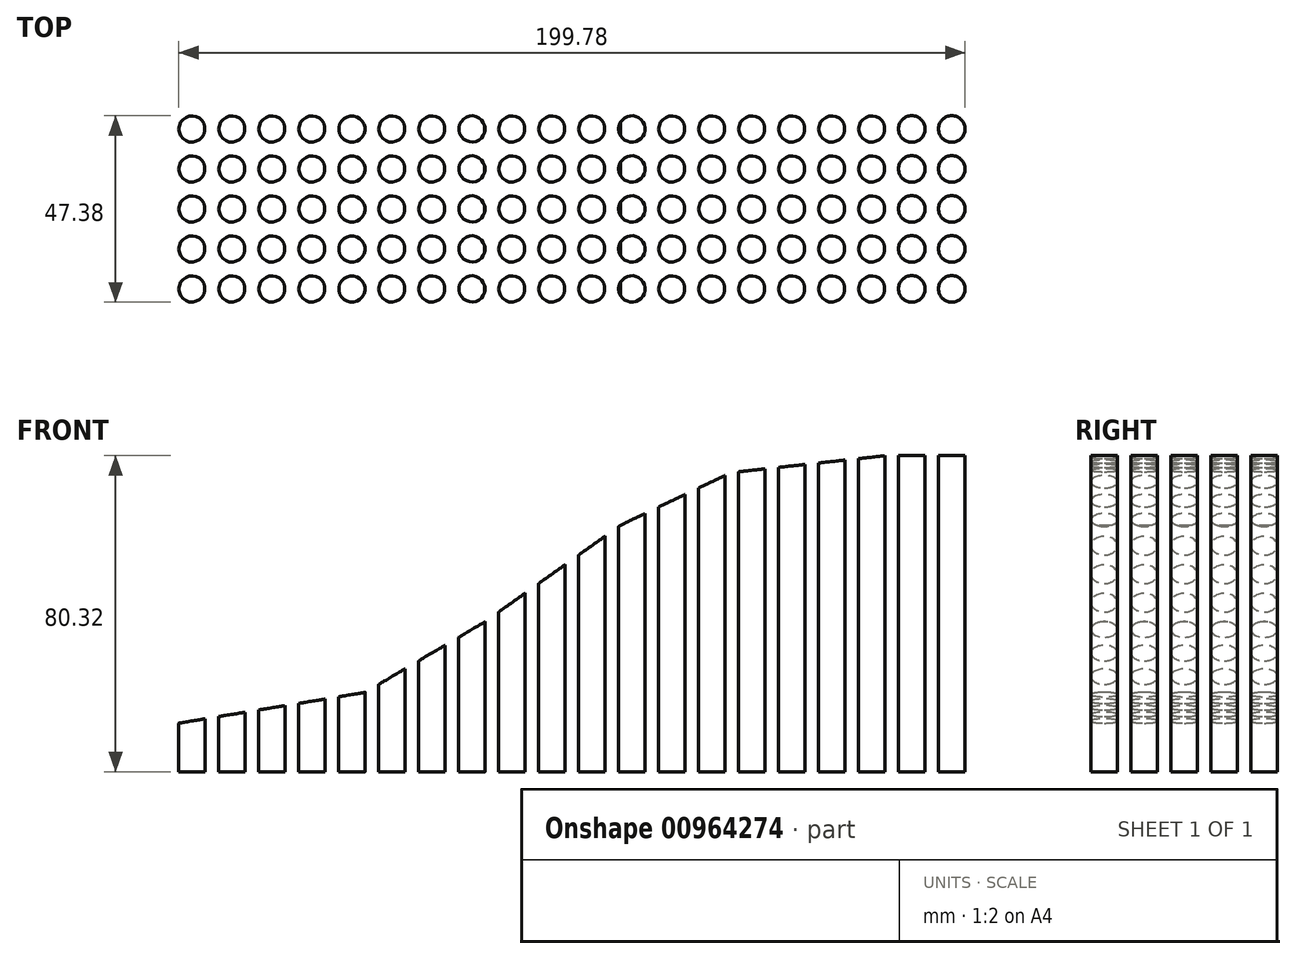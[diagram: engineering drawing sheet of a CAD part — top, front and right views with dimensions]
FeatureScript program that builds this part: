
annotation { "Feature Type Name" : "Feature", "Feature Type Description" : "" }
export const myFeature = defineFeature(function(context is Context, id is Id, definition is map)
    precondition{}
    {
        {
            var Q0;
            Q0=qCreatedBy(makeId("Top.planeOp"),FACE);
            var sketch = newSketch(context, id + "F0", { "sketchPlane" : qUnion([Q0])});
            skCircle(sketch, "E0", {"center": v(-70.77, 0) * mm, "radius": 3.37 * mm});
            skCircle(sketch, "E1.0.1.0", {"center": v(-70.77, 10.16) * mm, "radius": 3.37 * mm});
            skCircle(sketch, "E1.0.2.0", {"center": v(-70.77, 20.32) * mm, "radius": 3.37 * mm});
            skCircle(sketch, "E1.0.3.0", {"center": v(-70.77, 30.48) * mm, "radius": 3.37 * mm});
            skCircle(sketch, "E1.0.4.0", {"center": v(-70.77, 40.64) * mm, "radius": 3.37 * mm});
            skCircle(sketch, "E1.1.0.0", {"center": v(-60.61, 0) * mm, "radius": 3.37 * mm});
            skCircle(sketch, "E1.1.1.0", {"center": v(-60.61, 10.16) * mm, "radius": 3.37 * mm});
            skCircle(sketch, "E1.1.2.0", {"center": v(-60.61, 20.32) * mm, "radius": 3.37 * mm});
            skCircle(sketch, "E1.1.3.0", {"center": v(-60.61, 30.48) * mm, "radius": 3.37 * mm});
            skCircle(sketch, "E1.1.4.0", {"center": v(-60.61, 40.64) * mm, "radius": 3.37 * mm});
            skCircle(sketch, "E1.2.0.0", {"center": v(-50.45, 0) * mm, "radius": 3.37 * mm});
            skCircle(sketch, "E1.2.1.0", {"center": v(-50.45, 10.16) * mm, "radius": 3.37 * mm});
            skCircle(sketch, "E1.2.2.0", {"center": v(-50.45, 20.32) * mm, "radius": 3.37 * mm});
            skCircle(sketch, "E1.2.3.0", {"center": v(-50.45, 30.48) * mm, "radius": 3.37 * mm});
            skCircle(sketch, "E1.2.4.0", {"center": v(-50.45, 40.64) * mm, "radius": 3.37 * mm});
            skCircle(sketch, "E1.3.0.0", {"center": v(-40.3, 0) * mm, "radius": 3.37 * mm});
            skCircle(sketch, "E1.3.1.0", {"center": v(-40.3, 10.16) * mm, "radius": 3.37 * mm});
            skCircle(sketch, "E1.3.2.0", {"center": v(-40.3, 20.32) * mm, "radius": 3.37 * mm});
            skCircle(sketch, "E1.3.3.0", {"center": v(-40.3, 30.48) * mm, "radius": 3.37 * mm});
            skCircle(sketch, "E1.3.4.0", {"center": v(-40.3, 40.64) * mm, "radius": 3.37 * mm});
            skCircle(sketch, "E1.4.0.0", {"center": v(-30.13, 0) * mm, "radius": 3.37 * mm});
            skCircle(sketch, "E1.4.1.0", {"center": v(-30.13, 10.16) * mm, "radius": 3.37 * mm});
            skCircle(sketch, "E1.4.2.0", {"center": v(-30.13, 20.32) * mm, "radius": 3.37 * mm});
            skCircle(sketch, "E1.4.3.0", {"center": v(-30.13, 30.48) * mm, "radius": 3.37 * mm});
            skCircle(sketch, "E1.4.4.0", {"center": v(-30.13, 40.64) * mm, "radius": 3.37 * mm});
            skCircle(sketch, "E1.5.0.0", {"center": v(-19.97, 0) * mm, "radius": 3.37 * mm});
            skCircle(sketch, "E1.5.1.0", {"center": v(-19.97, 10.16) * mm, "radius": 3.37 * mm});
            skCircle(sketch, "E1.5.2.0", {"center": v(-19.97, 20.32) * mm, "radius": 3.37 * mm});
            skCircle(sketch, "E1.5.3.0", {"center": v(-19.97, 30.48) * mm, "radius": 3.37 * mm});
            skCircle(sketch, "E1.5.4.0", {"center": v(-19.97, 40.64) * mm, "radius": 3.37 * mm});
            skCircle(sketch, "E1.6.0.0", {"center": v(-9.81, 0) * mm, "radius": 3.37 * mm});
            skCircle(sketch, "E1.6.1.0", {"center": v(-9.81, 10.16) * mm, "radius": 3.37 * mm});
            skCircle(sketch, "E1.6.2.0", {"center": v(-9.81, 20.32) * mm, "radius": 3.37 * mm});
            skCircle(sketch, "E1.6.3.0", {"center": v(-9.81, 30.48) * mm, "radius": 3.37 * mm});
            skCircle(sketch, "E1.6.4.0", {"center": v(-9.81, 40.64) * mm, "radius": 3.37 * mm});
            skCircle(sketch, "E1.7.0.0", {"center": v(0.35, 0) * mm, "radius": 3.37 * mm});
            skCircle(sketch, "E1.7.1.0", {"center": v(0.35, 10.16) * mm, "radius": 3.37 * mm});
            skCircle(sketch, "E1.7.2.0", {"center": v(0.35, 20.32) * mm, "radius": 3.37 * mm});
            skCircle(sketch, "E1.7.3.0", {"center": v(0.35, 30.48) * mm, "radius": 3.37 * mm});
            skCircle(sketch, "E1.7.4.0", {"center": v(0.35, 40.64) * mm, "radius": 3.37 * mm});
            skCircle(sketch, "E1.8.0.0", {"center": v(10.5, 0) * mm, "radius": 3.37 * mm});
            skCircle(sketch, "E1.8.1.0", {"center": v(10.5, 10.16) * mm, "radius": 3.37 * mm});
            skCircle(sketch, "E1.8.2.0", {"center": v(10.5, 20.32) * mm, "radius": 3.37 * mm});
            skCircle(sketch, "E1.8.3.0", {"center": v(10.5, 30.48) * mm, "radius": 3.37 * mm});
            skCircle(sketch, "E1.8.4.0", {"center": v(10.5, 40.64) * mm, "radius": 3.37 * mm});
            skCircle(sketch, "E1.9.0.0", {"center": v(20.67, 0) * mm, "radius": 3.37 * mm});
            skCircle(sketch, "E1.9.1.0", {"center": v(20.67, 10.16) * mm, "radius": 3.37 * mm});
            skCircle(sketch, "E1.9.2.0", {"center": v(20.67, 20.32) * mm, "radius": 3.37 * mm});
            skCircle(sketch, "E1.9.3.0", {"center": v(20.67, 30.48) * mm, "radius": 3.37 * mm});
            skCircle(sketch, "E1.9.4.0", {"center": v(20.67, 40.64) * mm, "radius": 3.37 * mm});
            skCircle(sketch, "E1.10.0.0", {"center": v(30.83, 0) * mm, "radius": 3.37 * mm});
            skCircle(sketch, "E1.10.1.0", {"center": v(30.83, 10.16) * mm, "radius": 3.37 * mm});
            skCircle(sketch, "E1.10.2.0", {"center": v(30.83, 20.32) * mm, "radius": 3.37 * mm});
            skCircle(sketch, "E1.10.3.0", {"center": v(30.83, 30.48) * mm, "radius": 3.37 * mm});
            skCircle(sketch, "E1.10.4.0", {"center": v(30.83, 40.64) * mm, "radius": 3.37 * mm});
            skCircle(sketch, "E1.11.0.0", {"center": v(40.99, 0) * mm, "radius": 3.37 * mm});
            skCircle(sketch, "E1.11.1.0", {"center": v(40.99, 10.16) * mm, "radius": 3.37 * mm});
            skCircle(sketch, "E1.11.2.0", {"center": v(40.99, 20.32) * mm, "radius": 3.37 * mm});
            skCircle(sketch, "E1.11.3.0", {"center": v(40.99, 30.48) * mm, "radius": 3.37 * mm});
            skCircle(sketch, "E1.11.4.0", {"center": v(40.99, 40.64) * mm, "radius": 3.37 * mm});
            skCircle(sketch, "E1.12.0.0", {"center": v(51.15, 0) * mm, "radius": 3.37 * mm});
            skCircle(sketch, "E1.12.1.0", {"center": v(51.15, 10.16) * mm, "radius": 3.37 * mm});
            skCircle(sketch, "E1.12.2.0", {"center": v(51.15, 20.32) * mm, "radius": 3.37 * mm});
            skCircle(sketch, "E1.12.3.0", {"center": v(51.15, 30.48) * mm, "radius": 3.37 * mm});
            skCircle(sketch, "E1.12.4.0", {"center": v(51.15, 40.64) * mm, "radius": 3.37 * mm});
            skCircle(sketch, "E1.13.0.0", {"center": v(61.3, 0) * mm, "radius": 3.37 * mm});
            skCircle(sketch, "E1.13.1.0", {"center": v(61.3, 10.16) * mm, "radius": 3.37 * mm});
            skCircle(sketch, "E1.13.2.0", {"center": v(61.3, 20.32) * mm, "radius": 3.37 * mm});
            skCircle(sketch, "E1.13.3.0", {"center": v(61.3, 30.48) * mm, "radius": 3.37 * mm});
            skCircle(sketch, "E1.13.4.0", {"center": v(61.3, 40.64) * mm, "radius": 3.37 * mm});
            skCircle(sketch, "E1.14.0.0", {"center": v(71.47, 0) * mm, "radius": 3.37 * mm});
            skCircle(sketch, "E1.14.1.0", {"center": v(71.47, 10.16) * mm, "radius": 3.37 * mm});
            skCircle(sketch, "E1.14.2.0", {"center": v(71.47, 20.32) * mm, "radius": 3.37 * mm});
            skCircle(sketch, "E1.14.3.0", {"center": v(71.47, 30.48) * mm, "radius": 3.37 * mm});
            skCircle(sketch, "E1.14.4.0", {"center": v(71.47, 40.64) * mm, "radius": 3.37 * mm});
            skCircle(sketch, "E1.15.0.0", {"center": v(81.63, 0) * mm, "radius": 3.37 * mm});
            skCircle(sketch, "E1.15.1.0", {"center": v(81.63, 10.16) * mm, "radius": 3.37 * mm});
            skCircle(sketch, "E1.15.2.0", {"center": v(81.63, 20.32) * mm, "radius": 3.37 * mm});
            skCircle(sketch, "E1.15.3.0", {"center": v(81.63, 30.48) * mm, "radius": 3.37 * mm});
            skCircle(sketch, "E1.15.4.0", {"center": v(81.63, 40.64) * mm, "radius": 3.37 * mm});
            skCircle(sketch, "E1.16.0.0", {"center": v(91.79, 0) * mm, "radius": 3.37 * mm});
            skCircle(sketch, "E1.16.1.0", {"center": v(91.79, 10.16) * mm, "radius": 3.37 * mm});
            skCircle(sketch, "E1.16.2.0", {"center": v(91.79, 20.32) * mm, "radius": 3.37 * mm});
            skCircle(sketch, "E1.16.3.0", {"center": v(91.79, 30.48) * mm, "radius": 3.37 * mm});
            skCircle(sketch, "E1.16.4.0", {"center": v(91.79, 40.64) * mm, "radius": 3.37 * mm});
            skCircle(sketch, "E1.17.0.0", {"center": v(101.95, 0) * mm, "radius": 3.37 * mm});
            skCircle(sketch, "E1.17.1.0", {"center": v(101.95, 10.16) * mm, "radius": 3.37 * mm});
            skCircle(sketch, "E1.17.2.0", {"center": v(101.95, 20.32) * mm, "radius": 3.37 * mm});
            skCircle(sketch, "E1.17.3.0", {"center": v(101.95, 30.48) * mm, "radius": 3.37 * mm});
            skCircle(sketch, "E1.17.4.0", {"center": v(101.95, 40.64) * mm, "radius": 3.37 * mm});
            skCircle(sketch, "E1.18.0.0", {"center": v(112.1, 0) * mm, "radius": 3.37 * mm});
            skCircle(sketch, "E1.18.1.0", {"center": v(112.1, 10.16) * mm, "radius": 3.37 * mm});
            skCircle(sketch, "E1.18.2.0", {"center": v(112.1, 20.32) * mm, "radius": 3.37 * mm});
            skCircle(sketch, "E1.18.3.0", {"center": v(112.1, 30.48) * mm, "radius": 3.37 * mm});
            skCircle(sketch, "E1.18.4.0", {"center": v(112.1, 40.64) * mm, "radius": 3.37 * mm});
            skCircle(sketch, "E1.19.0.0", {"center": v(122.27, 0) * mm, "radius": 3.37 * mm});
            skCircle(sketch, "E1.19.1.0", {"center": v(122.27, 10.16) * mm, "radius": 3.37 * mm});
            skCircle(sketch, "E1.19.2.0", {"center": v(122.27, 20.32) * mm, "radius": 3.37 * mm});
            skCircle(sketch, "E1.19.3.0", {"center": v(122.27, 30.48) * mm, "radius": 3.37 * mm});
            skCircle(sketch, "E1.19.4.0", {"center": v(122.27, 40.64) * mm, "radius": 3.37 * mm});
            skLineSegment(sketch, "E1.direction1", {"start": v(-70.77, 0) * mm, "end": v(-60.61, 0) * mm, "construction": true});
            skLineSegment(sketch, "E1.direction2", {"start": v(-70.77, 0) * mm, "end": v(-70.77, 10.16) * mm, "construction": true});
            skSolve(sketch);
        }
        {
            var Q0;
            Q0=qCreatedBy(makeId("Front.planeOp"),FACE);
            var sketch = newSketch(context, id + "F1", { "sketchPlane" : qUnion([Q0])});
            skLineSegment(sketch, "E2", {"start": v(-76.38, 11.98) * mm, "end": v(-26.8, 20.18) * mm});
            skLineSegment(sketch, "E3", {"start": v(-26.8, 20.18) * mm, "end": v(3.6, 38.07) * mm});
            skLineSegment(sketch, "E4", {"start": v(3.6, 38.07) * mm, "end": v(38.1, 62.65) * mm});
            skLineSegment(sketch, "E5", {"start": v(38.1, 62.65) * mm, "end": v(66.12, 76.01) * mm});
            skLineSegment(sketch, "E6", {"start": v(66.12, 76.01) * mm, "end": v(105.36, 80.32) * mm});
            skLineSegment(sketch, "E7", {"start": v(105.36, 80.32) * mm, "end": v(127.56, 80.32) * mm});
            skLineSegment(sketch, "E8", {"start": v(-76.38, 11.98) * mm, "end": v(-90.5, 97.43) * mm});
            skLineSegment(sketch, "E9", {"start": v(-90.5, 97.43) * mm, "end": v(144.79, 106.16) * mm});
            skLineSegment(sketch, "E10", {"start": v(144.79, 106.16) * mm, "end": v(127.56, 80.32) * mm});
            skSolve(sketch);
        }
        {
            var Q0;
            Q0 = qSketchRegion(id + "F0", true);
            extrude(context, id + "F2", {"entities" : qUnion([Q0]), "depth" : 97.28 * mm, "offsetDistance" : 25.4 * mm});
        }
        {
            var Q0;
            Q0=makeQuery(id+"F1.imprint","IMPRINT",FACE,{"disambiguationData":[TD([[makeQuery(id+"F1.imprint","IMPRINT",EDGE,{"derivedFrom":sQuery(id+"F1.wireOp",EDGE,"E2")}),1.0]])]});
            extrude(context, id + "F3", {"entities" : qUnion([Q0]), "operationType" : NewBodyOperationType.REMOVE, "oppositeDirection" : true, "depth" : 66.55 * mm, "offsetDistance" : 25.4 * mm, "hasSecondDirection" : true, "secondDirectionOppositeDirection" : false, "secondDirectionDepth" : 25.4 * mm});
        }
    });
